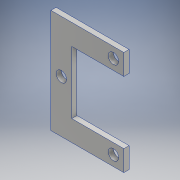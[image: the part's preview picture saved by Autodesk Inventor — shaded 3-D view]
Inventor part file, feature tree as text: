
AUTODESK INVENTOR PART (.ipt)
format: ipt  version: 2018.1 (Build 221171000, 171)  size: 122,880 bytes
history: native  units: mm
features: extrude x2, sketch x2, other x1
ambient origin geometry x8: Origin, YZ Plane, XZ Plane, XY Plane, X Axis, Y Axis, Z Axis, Center Point
bodies: Body1 (feature_tree)
feature tree (5):
  other  "ソリッド1"
  extrude  "押し出し1"  Depth=20.0mm
  extrude  "押し出し2"  Depth=50.0mm
  sketch  "スケッチ1"
  sketch  "スケッチ2"
